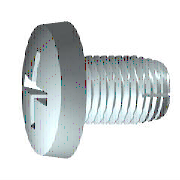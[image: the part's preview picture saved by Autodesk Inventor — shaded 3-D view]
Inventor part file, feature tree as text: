
AUTODESK INVENTOR PART (.ipt)
format: ipt  version: 2024.1 (Build 281209000, 209)  size: 287,744 bytes
history: native  units: mm (DEFAULTED — no unit token found)
features: other x2, extrude x1, plane x1
ambient origin geometry x8: Origin, YZ Plane, XZ Plane, XY Plane, X Axis, Y Axis, Z Axis, Center Point
bodies: Solid1 (feature_tree), Body (feature_tree)
feature tree (4):
  other  "IDS_WORKPLANE{1}"
  extrude  "Slot"  Depth=3.0mm
  other  "Cut"
  plane  "Work Plane3"
